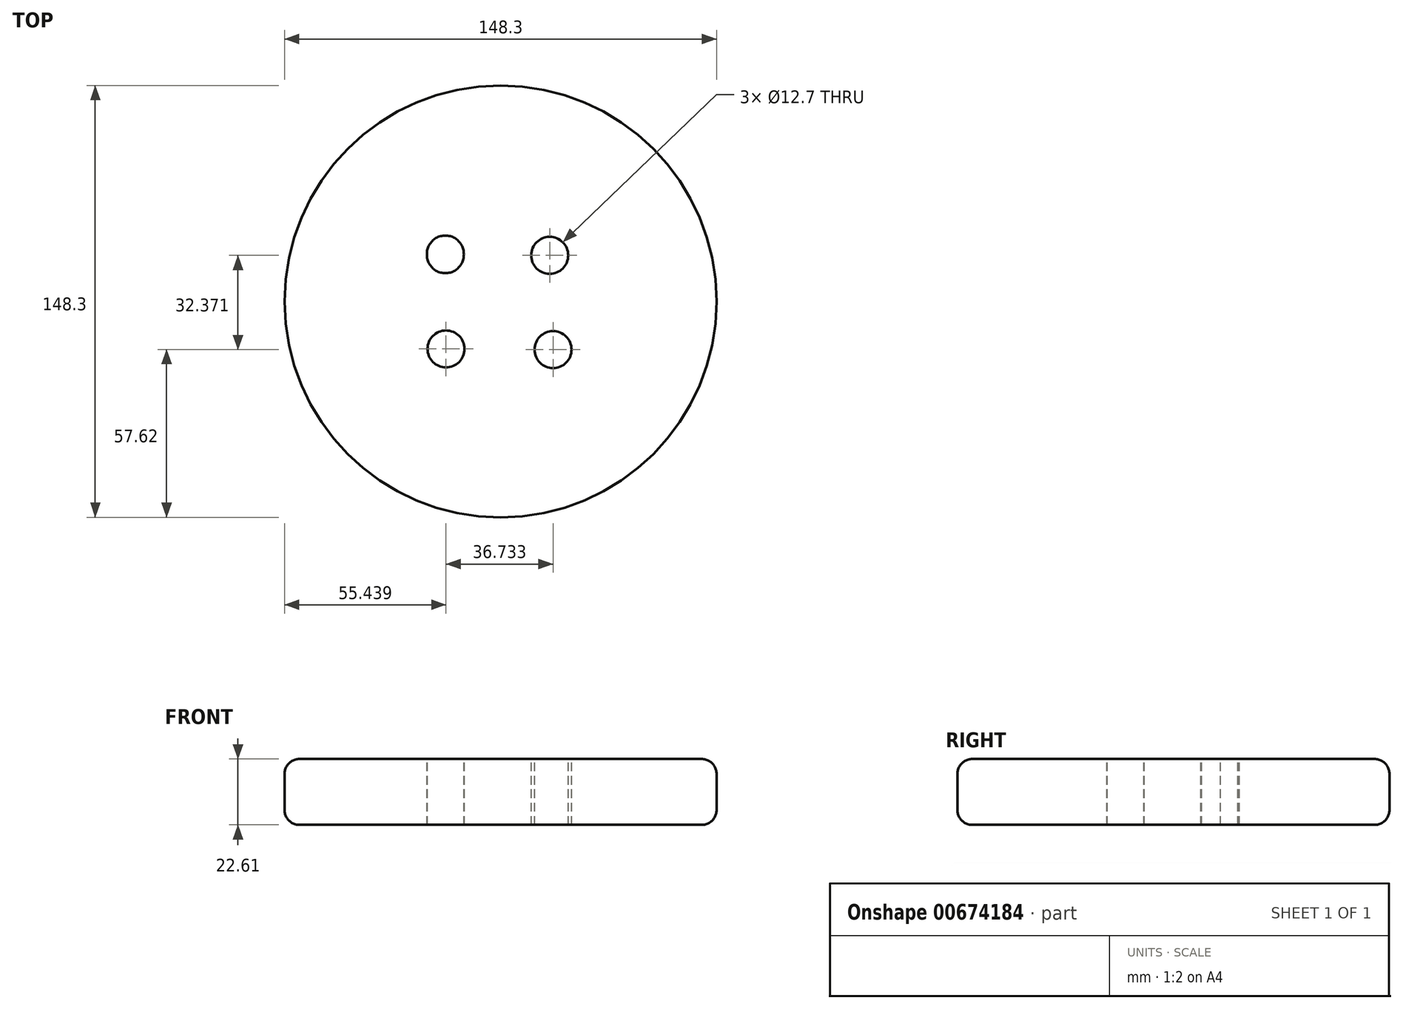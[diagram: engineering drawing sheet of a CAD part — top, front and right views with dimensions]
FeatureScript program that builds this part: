
annotation { "Feature Type Name" : "Feature", "Feature Type Description" : "" }
export const myFeature = defineFeature(function(context is Context, id is Id, definition is map)
    precondition{}
    {
        {
            var Q0;
            Q0=qCreatedBy(makeId("Top.planeOp"),FACE);
            var sketch = newSketch(context, id + "F0", { "sketchPlane" : qUnion([Q0])});
            skCircle(sketch, "E0", {"center": v(0, 0) * mm, "radius": 75.72 * mm});
            skCircle(sketch, "E1", {"center": v(0, 0) * mm, "radius": 74.15 * mm});
            skLineSegment(sketch, "E2", {"start": v(0, 74.15) * mm, "end": v(0, 0) * mm});
            skLineSegment(sketch, "E3", {"start": v(0, 0) * mm, "end": v(51.78, -53.08) * mm});
            skLineSegment(sketch, "E4", {"start": v(0, 0) * mm, "end": v(-53.08, -51.78) * mm});
            skLineSegment(sketch, "E5", {"start": v(0, 0) * mm, "end": v(53.08, 51.78) * mm});
            skLineSegment(sketch, "E6", {"start": v(0, 0) * mm, "end": v(0, -74.15) * mm});
            skLineSegment(sketch, "E7", {"start": v(0, 0) * mm, "end": v(74.15, 0) * mm});
            skLineSegment(sketch, "E8", {"start": v(0, 0) * mm, "end": v(-74.15, 0) * mm});
            skLineSegment(sketch, "E9", {"start": v(0, 0) * mm, "end": v(-51.78, 53.08) * mm});
            skSolve(sketch);
        }
        {
            var Q0;
            {var subQ0=sQuery(id+"F0.wireOp",EDGE,"E3");Q0=makeQuery(id+"F0.imprint","IMPRINT",FACE,{"disambiguationData":[TD([[makeQuery(id+"F0.imprint","IMPRINT",EDGE,{"derivedFrom":subQ0}),-1.0]])]});}
            var Q1;
            {var subQ0=sQuery(id+"F0.wireOp",EDGE,"E3");Q1=makeQuery(id+"F0.imprint","IMPRINT",FACE,{"disambiguationData":[TD([[makeQuery(id+"F0.imprint","IMPRINT",EDGE,{"derivedFrom":subQ0}),1.0]])]});}
            var Q2;
            {var subQ0=sQuery(id+"F0.wireOp",EDGE,"E5");Q2=makeQuery(id+"F0.imprint","IMPRINT",FACE,{"disambiguationData":[TD([[makeQuery(id+"F0.imprint","IMPRINT",EDGE,{"derivedFrom":subQ0}),-1.0]])]});}
            var Q3;
            {var subQ0=sQuery(id+"F0.wireOp",EDGE,"E2");Q3=makeQuery(id+"F0.imprint","IMPRINT",FACE,{"disambiguationData":[TD([[makeQuery(id+"F0.imprint","IMPRINT",EDGE,{"derivedFrom":subQ0}),1.0]])]});}
            var Q4;
            {var subQ0=sQuery(id+"F0.wireOp",EDGE,"E2");Q4=makeQuery(id+"F0.imprint","IMPRINT",FACE,{"disambiguationData":[TD([[makeQuery(id+"F0.imprint","IMPRINT",EDGE,{"derivedFrom":subQ0}),-1.0]])]});}
            var Q5;
            {var subQ0=sQuery(id+"F0.wireOp",EDGE,"E8");Q5=makeQuery(id+"F0.imprint","IMPRINT",FACE,{"disambiguationData":[TD([[makeQuery(id+"F0.imprint","IMPRINT",EDGE,{"derivedFrom":subQ0}),-1.0]])]});}
            var Q6;
            {var subQ0=sQuery(id+"F0.wireOp",EDGE,"E4");Q6=makeQuery(id+"F0.imprint","IMPRINT",FACE,{"disambiguationData":[TD([[makeQuery(id+"F0.imprint","IMPRINT",EDGE,{"derivedFrom":subQ0}),-1.0]])]});}
            var Q7;
            {var subQ0=sQuery(id+"F0.wireOp",EDGE,"E4");Q7=makeQuery(id+"F0.imprint","IMPRINT",FACE,{"disambiguationData":[TD([[makeQuery(id+"F0.imprint","IMPRINT",EDGE,{"derivedFrom":subQ0}),1.0]])]});}
            extrude(context, id + "F1", {"entities" : qUnion([Q0, Q1, Q2, Q3, Q4, Q5, Q6, Q7]), "depth" : 22.6 * mm, "offsetDistance" : 25.4 * mm});
        }
        {
            var Q0;
            Q0=makeQuery(id+"F1.opExtrude","CAP_EDGE",EDGE,{"disambiguationData":[OSD([sQuery(id+"F0.wireOp",EDGE,"E1")])],"isStart":false});
            var Q1;
            Q1=makeQuery(id+"F1.opExtrude","CAP_EDGE",EDGE,{"disambiguationData":[OSD([sQuery(id+"F0.wireOp",EDGE,"E1")])],"isStart":true});
            fillet(context, id + "F2", {"entities" : qUnion([Q0, Q1]), "radius" : 5.08 * mm, "tangentPropagation" : true, "allowEdgeOverflow" : false});
        }
        {
            var Q0;
            Q0=makeQuery(id+"F1.opExtrude","CAP_FACE",FACE,{"disambiguationData":[OSD([sQuery(id+"F0.wireOp",EDGE,"E1")])],"isStart":false});
            var sketch = newSketch(context, id + "F3", { "sketchPlane" : qUnion([Q0])});
            skCircle(sketch, "E10", {"center": v(-18.94, 16.07) * mm, "radius": 7 * mm});
            skCircle(sketch, "E11", {"center": v(16.87, 15.84) * mm, "radius": 6.89 * mm});
            skCircle(sketch, "E12", {"center": v(-18.71, -16.3) * mm, "radius": 7.47 * mm});
            skCircle(sketch, "E13", {"center": v(17.8, -16.3) * mm, "radius": 7.2 * mm});
            skCircle(sketch, "E14", {"center": v(16.87, 15.84) * mm, "radius": 7.32 * mm});
            skSolve(sketch);
        }
        {
            var Q0;
            Q0=makeQuery(id+"F3.imprint","IMPRINT",FACE,{"disambiguationData":[TD([[makeQuery(id+"F3.imprint","IMPRINT",EDGE,{"derivedFrom":sQuery(id+"F3.wireOp",EDGE,"E10")}),-1.0]])]});
            var sketch = newSketch(context, id + "F4", { "sketchPlane" : qUnion([Q0])});
            skCircle(sketch, "E15", {"center": v(-18.94, 16.3) * mm, "radius": 7.26 * mm});
            skCircle(sketch, "E16", {"center": v(-18.71, -16.3) * mm, "radius": 7 * mm});
            skCircle(sketch, "E17", {"center": v(18.02, -16.53) * mm, "radius": 6.81 * mm});
            skSolve(sketch);
        }
        {
            var Q0;
            Q0=sQuery(id+"F3.wireOp",VERTEX,"E10.center");
            var Q1;
            Q1=sQuery(id+"F3.wireOp",VERTEX,"E11.center");
            var Q2;
            Q2=sQuery(id+"F4.wireOp",VERTEX,"E17.center");
            var Q3;
            Q3=sQuery(id+"F3.wireOp",VERTEX,"E12.center");
            var Q4;
            Q4=sQuery(id+"F4.wireOp",VERTEX,"E15.center");
            var Q5;
            Q5=makeQuery(id+"F1.opExtrude","SWEPT_BODY",BODY,{"disambiguationData":[OSD([sQuery(id+"F0.wireOp",EDGE,"E1")])]});
            hole(context, id + "F5", {"style" : HoleStyle.SIMPLE, "endStyle" : HoleEndStyle.THROUGH, "holeDiameter" : 12.7 * mm, "majorDiameter" : 6.35 * mm, "isTappedThrough" : true, "tappedDepth" : 12.7 * mm, "tapClearance" : 3, "locations" : qUnion([Q0, Q1, Q2, Q3, Q4]), "scope" : qUnion([Q5])});
        }
    });
